FCSTD DOCUMENT  (FreeCAD 0.16RUnknown)
Label: hook
License: All rights reserved
LicenseURL: http://en.wikipedia.org/wiki/All_rights_reserved
objects: Sketcher::SketchObject×1
note: 1 computed .brp shape members not serialized (recipe doc carries the construction recipe); baked Part::Feature solids carry a one-line shape summary decoded from their .brp

FEATURE [Sketcher::SketchObject] Sketch
  sketch-geometry (8):
    g0: LineSegment StartX=0 StartY=-17.7841 StartZ=0 EndX=3 EndY=-17.7841 EndZ=0
    g1: LineSegment StartX=3 StartY=-17.7841 StartZ=0 EndX=3 EndY=-22.7841 EndZ=0
    g2: LineSegment StartX=3 StartY=-22.7841 StartZ=0 EndX=0 EndY=-22.7841 EndZ=0
    g3: LineSegment StartX=0 StartY=-22.7841 StartZ=0 EndX=0 EndY=-21.2841 EndZ=0
    g4: LineSegment StartX=0 StartY=-19.2841 StartZ=0 EndX=1.5 EndY=-19.2841 EndZ=0
    g5: LineSegment StartX=1.5 StartY=-19.2841 StartZ=0 EndX=1.5 EndY=-21.2841 EndZ=0
    g6: LineSegment StartX=1.5 StartY=-21.2841 StartZ=0 EndX=0 EndY=-21.2841 EndZ=0
    g7: LineSegment StartX=0 StartY=-19.2841 StartZ=0 EndX=0 EndY=-17.7841 EndZ=0
  constraints (22):
    c: Coincident(g0,g1)
    c: Coincident(g1,g2)
    c: Coincident(g2,g3)
    c: Coincident(g7,g0)
    c: Horizontal(g0)
    c: Horizontal(g2)
    c: Vertical(g1)
    c: Vertical(g3)
    c: PointOnObject(g0,g-2)
    c: Coincident(g4,g5)
    c: Coincident(g5,g6)
    c: Horizontal(g4)
    c: Horizontal(g6)
    c: Vertical(g5)
    c: Coincident(g7,g4)
    c: Tangent(g3,g7)
    c: Coincident(g6,g3)
    c: DistanceX(g2,g2) = 3
    c: DistanceX(g6,g6) = 1.5
    c: DistanceY(g1,g1) = 5
    c: Equal(g7,g3)
    c: DistanceY(g7,g7) = 1.5
